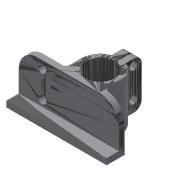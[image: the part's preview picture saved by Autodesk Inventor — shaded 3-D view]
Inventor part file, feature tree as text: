
AUTODESK INVENTOR PART (.ipt)
format: ipt  version: 2017 (Build 210142000, 142)  size: 622,592 bytes
history: native  units: mm
features: other x3, sketch x3, projected_geometry x2, extrude x1, hole x1
ambient origin geometry x8: Origin, YZ Plane, XZ Plane, XY Plane, X Axis, Y Axis, Z Axis, Center Point
bodies: Solid1 (feature_tree)
feature tree (10):
  other  "Z Endstop Holder"
  other  "MeshFeature1:1"
  sketch  "Sketch1"  dims[d0=12.0mm d1=10.0mm d2=0.0mm]
  extrude  "Extrusion1"  Depth=10.0mm TaperAngle=0.0deg
  hole  "Hole1"  [1 undecoded]
  sketch  "Sketch2"  dims[d3=3.3mm d4=6.0mm d5=4.0mm d6=2.0mm d7=90.0deg d8=8.0mm d9=20.594885mm]
  projected_geometry  "Projected Loop1"
  sketch  "Sketch3"
  projected_geometry  "Projected Loop2"
  other  "MeshFeature1"
note: 1 required parameter value undecoded (feature->parameter linkage not recoverable at this tier; creation-order binding heuristic only, values carry confidence <= 0.55)
